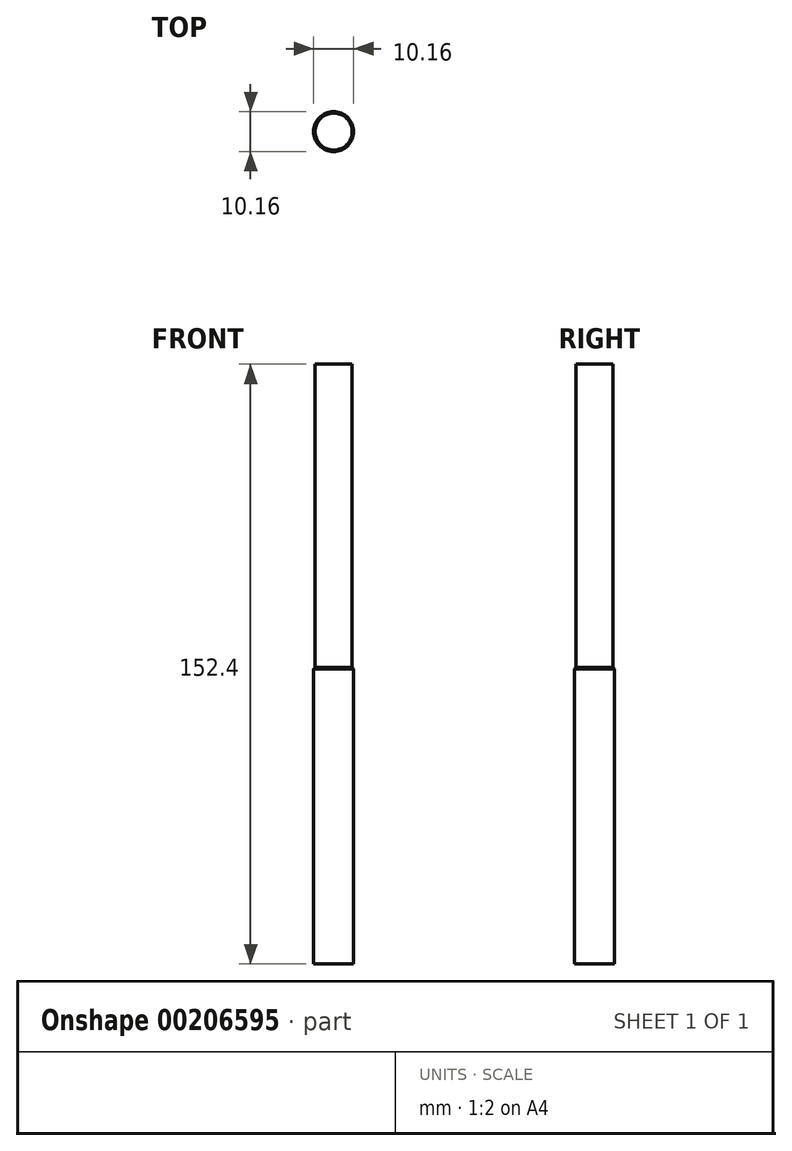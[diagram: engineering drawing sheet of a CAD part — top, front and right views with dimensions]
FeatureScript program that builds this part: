
annotation { "Feature Type Name" : "Feature", "Feature Type Description" : "" }
export const myFeature = defineFeature(function(context is Context, id is Id, definition is map)
    precondition{}
    {
        {
            var Q0;
            Q0=qCreatedBy(makeId("Top.planeOp"),FACE);
            var sketch = newSketch(context, id + "F0", { "sketchPlane" : qUnion([Q0])});
            skCircle(sketch, "E0", {"center": v(0, 0) * mm, "radius": 5.08 * mm});
            skSolve(sketch);
        }
        {
            var Q0;
            Q0=makeQuery(id+"F0.imprint","IMPRINT",FACE,{"disambiguationData":[TD([[makeQuery(id+"F0.imprint","IMPRINT",EDGE,{"derivedFrom":sQuery(id+"F0.wireOp",EDGE,"E0")}),1.0]])]});
            var Q1;
            Q1=sQuery(id+"F0.wireOp",EDGE,"E0");
            extrude(context, id + "F1", {"entities" : qUnion([Q0]), "surfaceEntities" : qUnion([Q1]), "oppositeDirection" : true, "depth" : 76.2 * mm});
        }
        {
            var Q0;
            Q0=makeQuery(id+"F1.opExtrude","CAP_FACE",FACE,{"disambiguationData":[OSD([sQuery(id+"F0.wireOp",EDGE,"E0")])],"isStart":true});
            var sketch = newSketch(context, id + "F2", { "sketchPlane" : qUnion([Q0])});
            skCircle(sketch, "E1", {"center": v(0, 0) * mm, "radius": 4.7 * mm});
            skSolve(sketch);
        }
        {
            var Q0;
            Q0=makeQuery(id+"F2.imprint","IMPRINT",FACE,{"disambiguationData":[TD([[makeQuery(id+"F2.imprint","IMPRINT",EDGE,{"derivedFrom":sQuery(id+"F2.wireOp",EDGE,"E1")}),1.0]])]});
            var Q1;
            Q1=sQuery(id+"F2.wireOp",EDGE,"E1");
            extrude(context, id + "F3", {"entities" : qUnion([Q0]), "operationType" : NewBodyOperationType.ADD, "surfaceEntities" : qUnion([Q1]), "depth" : 76.2 * mm});
        }
        {
            var Q0;
            Q0=makeQuery(id+"F1.opExtrude","CAP_EDGE",EDGE,{"disambiguationData":[OSD([sQuery(id+"F0.wireOp",EDGE,"E0")])],"isStart":true});
            chamfer(context, id + "F4", {"entities" : qUnion([Q0]), "width" : 1.27 * mm, "tangentPropagation" : true});
        }
    });
